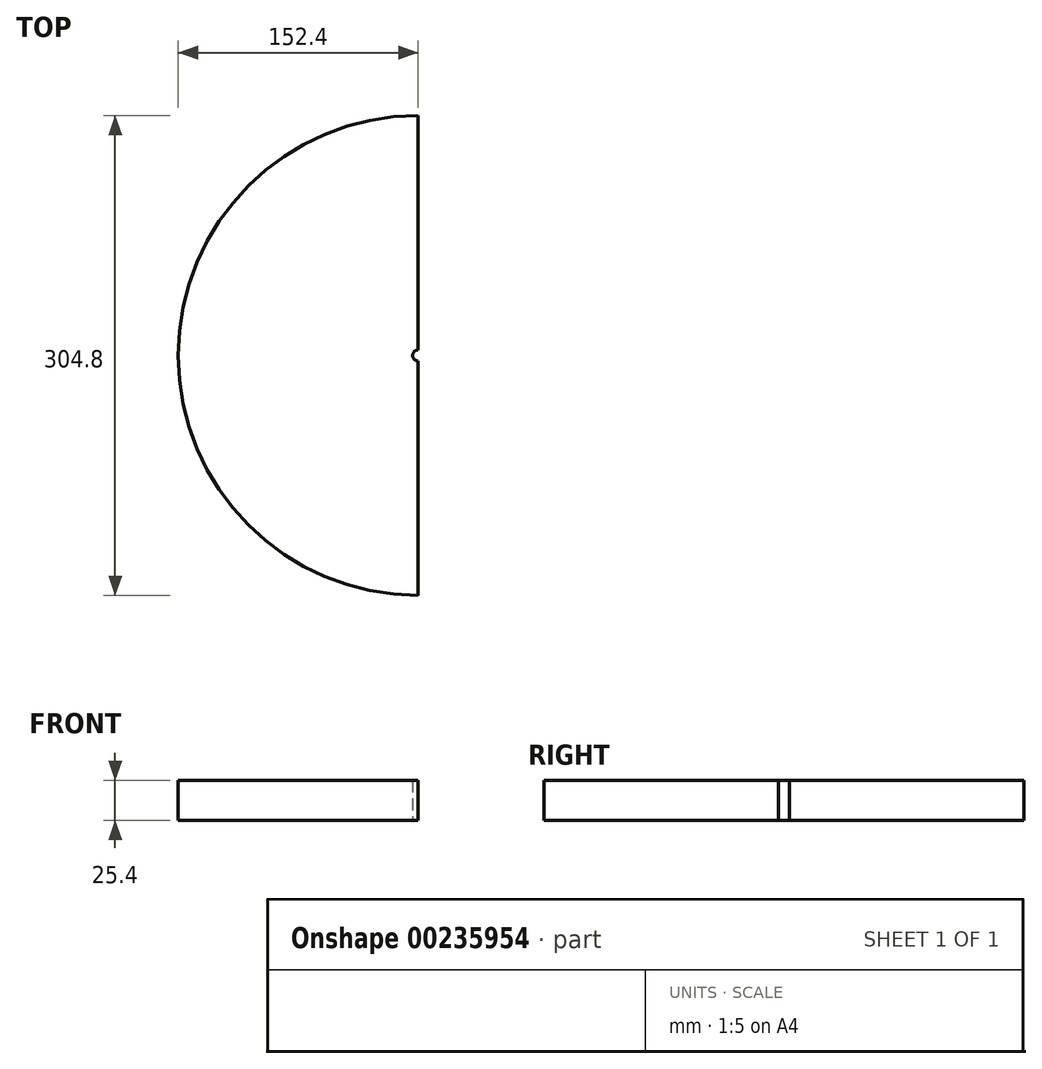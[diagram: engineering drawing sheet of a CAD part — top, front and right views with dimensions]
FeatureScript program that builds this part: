
annotation { "Feature Type Name" : "Feature", "Feature Type Description" : "" }
export const myFeature = defineFeature(function(context is Context, id is Id, definition is map)
    precondition{}
    {
        {
            var Q0;
            Q0=qCreatedBy(makeId("Top.planeOp"),FACE);
            var sketch = newSketch(context, id + "F0", { "sketchPlane" : qUnion([Q0])});
            skCircle(sketch, "E0", {"center": v(-26.2, 8.77) * mm, "radius": 152.4 * mm});
            skCircle(sketch, "E1", {"center": v(-26.2, 8.77) * mm, "radius": 3.5 * mm});
            skLineSegment(sketch, "E2", {"start": v(-26.2, 8.77) * mm, "end": v(-26.2, 161.17) * mm});
            skLineSegment(sketch, "E3", {"start": v(-26.2, 8.77) * mm, "end": v(-26.2, -143.63) * mm});
            skSolve(sketch);
        }
        {
            var Q0;
            {var subQ0=sQuery(id+"F0.wireOp",EDGE,"E2");var subQ1=sQuery(id+"F0.wireOp",EDGE,"E0");var subQ2=makeQuery(id+"F0.imprint","INTERSECT",VERTEX,{"derivedFrom":[subQ1,subQ0]});Q0=makeQuery(id+"F0.imprint","IMPRINT",FACE,{"disambiguationData":[TD([[makeQuery(id+"F0.imprint","IMPRINT",EDGE,{"disambiguationData":[TD([[subQ2,-1.0]])],"derivedFrom":subQ1}),1.0]])]});}
            extrude(context, id + "F1", {"entities" : qUnion([Q0]), "depth" : 25.4 * mm});
        }
    });
